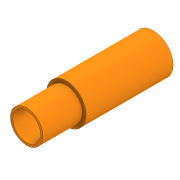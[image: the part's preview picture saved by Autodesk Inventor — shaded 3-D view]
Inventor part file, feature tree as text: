
AUTODESK INVENTOR PART (.ipt)
format: ipt  version: 2020 (Build 240168000, 168)  size: 94,208 bytes
history: native  units: in
note: dims shown in document units (in); Inventor stores cm internally (conversion verified against a paired STEP export)
features: extrude x2, sketch x2
ambient origin geometry x8: Origin, YZ Plane, XZ Plane, XY Plane, X Axis, Y Axis, Z Axis, Center Point
bodies: Solid1 (feature_tree)
feature tree (4):
  extrude  "Extrusion1"  Depth=0.7874in
  extrude  "Extrusion2"  Depth=0.7874in
  sketch  "Sketch1"  dims[d0=0.7874in d1=0.5512in]
  sketch  "Sketch2"  dims[d2=2.5197in d3=0.0in d4=0.0689in d5=0.7874in d6=0.0in]
